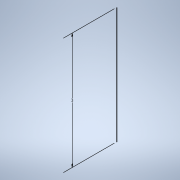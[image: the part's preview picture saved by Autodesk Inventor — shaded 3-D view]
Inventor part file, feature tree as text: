
AUTODESK INVENTOR PART (.ipt)
format: ipt  version: 2022 (Build 260153000, 153)  size: 201,216 bytes
history: native  units: mm
features: other x1, revolve x1, fillet x1, sketch x1
ambient origin geometry x8: Origin, YZ Plane, XZ Plane, XY Plane, X Axis, Y Axis, Z Axis, Center Point
bodies: Body1 (feature_tree)
feature tree (4):
  other  "Твердое тело1"
  revolve  "Вращение1"
  fillet  "Сопряжение1"  Radius=3.0mm
  sketch  "Эскиз1"
